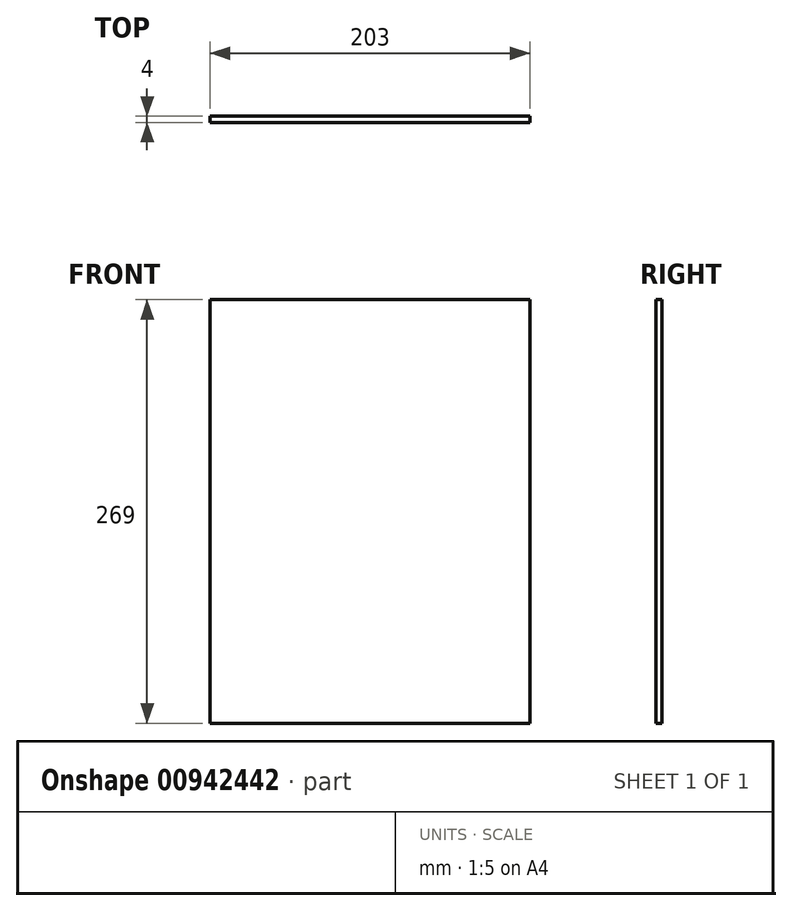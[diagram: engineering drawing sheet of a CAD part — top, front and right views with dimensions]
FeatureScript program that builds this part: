
annotation { "Feature Type Name" : "Feature", "Feature Type Description" : "" }
export const myFeature = defineFeature(function(context is Context, id is Id, definition is map)
    precondition{}
    {
        {
            var Q0;
            Q0=qCreatedBy(makeId("Front.planeOp"),FACE);
            var sketch = newSketch(context, id + "F0", { "sketchPlane" : qUnion([Q0])});
            skLineSegment(sketch, "E0.bottom", {"start": v(0, 0) * mm, "end": v(-203, 0) * mm});
            skLineSegment(sketch, "E0.top", {"start": v(0, 269) * mm, "end": v(-203, 269) * mm});
            skLineSegment(sketch, "E0.left", {"start": v(0, 0) * mm, "end": v(0, 269) * mm});
            skLineSegment(sketch, "E0.right", {"start": v(-203, 0) * mm, "end": v(-203, 269) * mm});
            skSolve(sketch);
        }
        {
            var Q0;
            Q0 = qSketchRegion(id + "F0", true);
            extrude(context, id + "F1", {"entities" : qUnion([Q0]), "depth" : 4 * mm, "offsetDistance" : 25 * mm});
        }
    });
